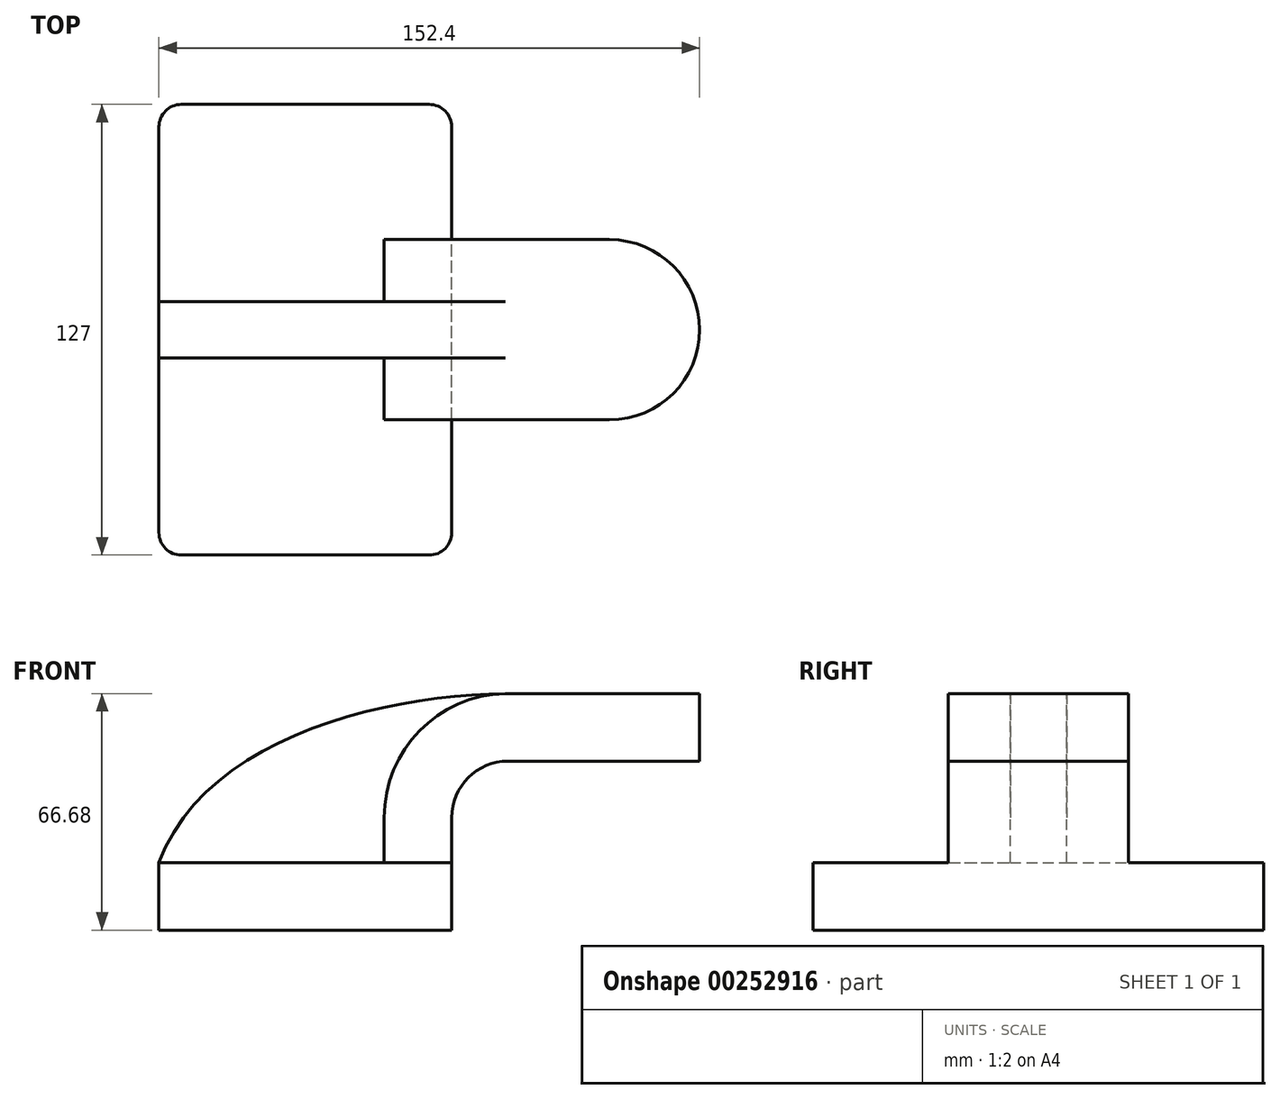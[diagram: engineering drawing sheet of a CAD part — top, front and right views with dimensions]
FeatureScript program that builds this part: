
annotation { "Feature Type Name" : "Feature", "Feature Type Description" : "" }
export const myFeature = defineFeature(function(context is Context, id is Id, definition is map)
    precondition{}
    {
        {
            var Q0;
            Q0=qCreatedBy(makeId("Front.planeOp"),FACE);
            var sketch = newSketch(context, id + "F0", { "sketchPlane" : qUnion([Q0])});
            skLineSegment(sketch, "E0.bottom", {"start": v(41.28, -9.52) * mm, "end": v(-41.28, -9.53) * mm});
            skLineSegment(sketch, "E0.top", {"start": v(41.28, 9.53) * mm, "end": v(-41.28, 9.53) * mm});
            skLineSegment(sketch, "E0.left", {"start": v(41.28, -9.52) * mm, "end": v(41.28, 9.53) * mm});
            skLineSegment(sketch, "E0.right", {"start": v(-41.28, -9.53) * mm, "end": v(-41.28, 9.53) * mm});
            skPoint(sketch, "E0.middle", {"position": v(0, 0) * mm});
            skLineSegment(sketch, "E1.bottom", {"start": v(111.13, 38.1) * mm, "end": v(60.33, 38.1) * mm});
            skLineSegment(sketch, "E1.top", {"start": v(111.13, 66.68) * mm, "end": v(60.33, 66.68) * mm});
            skLineSegment(sketch, "E1.left", {"start": v(111.13, 38.1) * mm, "end": v(111.13, 66.68) * mm});
            skLineSegment(sketch, "E1.right", {"start": v(60.33, 38.1) * mm, "end": v(60.33, 66.67) * mm});
            skPoint(sketch, "E1.middle", {"position": v(85.73, 52.39) * mm});
            skLineSegment(sketch, "E2", {"start": v(41.28, 9.53) * mm, "end": v(41.28, 22.23) * mm});
            skArc(sketch, "E3", {"start": v(41.27, 22.23) * mm, "mid": v(45.92, 33.45) * mm, "end": v(57.15, 38.1) * mm});
            skLineSegment(sketch, "E4", {"start": v(57.15, 38.1) * mm, "end": v(80.61, 38.1) * mm});
            skLineSegment(sketch, "E5.0", {"start": v(57.15, 57.15) * mm, "end": v(80.61, 57.15) * mm});
            skArc(sketch, "E5.1", {"start": v(22.22, 22.23) * mm, "mid": v(32.45, 46.92) * mm, "end": v(57.15, 57.15) * mm});
            skLineSegment(sketch, "E5.2", {"start": v(22.22, 9.53) * mm, "end": v(22.22, 22.23) * mm});
            skFitSpline(sketch, "E6", {"points": [v(-41.28, 9.53) * mm, v(57.15, 57.15) * mm], "startDerivative": vector(39.74, 106.1) * mm, "endDerivative": vector(104.57, 0.93) * mm});
            skLineSegment(sketch, "E7", {"start": v(85.73, 66.68) * mm, "end": v(85.73, 38.1) * mm});
            skLineSegment(sketch, "E8", {"start": v(80.61, 57.15) * mm, "end": v(85.73, 57.15) * mm});
            skLineSegment(sketch, "E9", {"start": v(80.61, 38.1) * mm, "end": v(85.73, 38.1) * mm});
            skSolve(sketch);
        }
        {
            var Q0;
            Q0=makeQuery(id+"F0.imprint","IMPRINT",FACE,{"disambiguationData":[TD([[makeQuery(id+"F0.imprint","IMPRINT",EDGE,{"derivedFrom":sQuery(id+"F0.wireOp",EDGE,"E0.bottom")}),-1.0]])]});
            extrude(context, id + "F1", {"entities" : qUnion([Q0]), "endBound" : BoundingType.SYMMETRIC, "depth" : 127 * mm});
        }
        {
            var Q0;
            {var subQ3=sQuery(id+"F0.wireOp",EDGE,"E5.2");Q0=makeQuery(id+"F0.imprint","IMPRINT",FACE,{"disambiguationData":[TD([[makeQuery(id+"F0.imprint","IMPRINT",EDGE,{"derivedFrom":subQ3}),1.0]])]});}
            extrude(context, id + "F2", {"entities" : qUnion([Q0]), "operationType" : NewBodyOperationType.ADD, "endBound" : BoundingType.SYMMETRIC, "depth" : 15.88 * mm});
        }
        {
            var Q0;
            {var subQ1=sQuery(id+"F0.wireOp",EDGE,"E2");Q0=makeQuery(id+"F0.imprint","IMPRINT",FACE,{"disambiguationData":[TD([[makeQuery(id+"F0.imprint","IMPRINT",EDGE,{"derivedFrom":subQ1}),1.0]])]});}
            var Q1;
            {var subQ2=sQuery(id+"F0.wireOp",EDGE,"E8");Q1=makeQuery(id+"F0.imprint","IMPRINT",FACE,{"disambiguationData":[TD([[makeQuery(id+"F0.imprint","IMPRINT",EDGE,{"derivedFrom":subQ2}),-1.0]])]});}
            extrude(context, id + "F3", {"entities" : qUnion([Q0, Q1]), "operationType" : NewBodyOperationType.ADD, "endBound" : BoundingType.SYMMETRIC, "depth" : 50.8 * mm});
        }
        {
            var Q0;
            {var subQ5=sQuery(id+"F0.wireOp",EDGE,"E1.bottom");Q0=makeQuery(id+"F0.imprint","IMPRINT",FACE,{"disambiguationData":[TD([[makeQuery(id+"F0.imprint","IMPRINT",EDGE,{"derivedFrom":subQ5}),-1.0]])]});}
            var Q1;
            Q1=sQuery(id+"F0.wireOp",EDGE,"E7");
            revolve(context, id + "F4", {"operationType" : NewBodyOperationType.ADD, "entities" : qUnion([Q0]), "axis" : qUnion([Q1]), "revolveType" : RevolveType.FULL});
        }
        {
            var Q0;
            Q0=makeQuery(id+"F1.opExtrude","CAP_EDGE",EDGE,{"disambiguationData":[OSD([sQuery(id+"F0.wireOp",EDGE,"E0.left")])],"isStart":false});
            var Q1;
            Q1=makeQuery(id+"F1.opExtrude","CAP_EDGE",EDGE,{"disambiguationData":[OSD([sQuery(id+"F0.wireOp",EDGE,"E0.right")])],"isStart":false});
            var Q2;
            Q2=makeQuery(id+"F1.opExtrude","CAP_EDGE",EDGE,{"disambiguationData":[OSD([sQuery(id+"F0.wireOp",EDGE,"E0.right")])],"isStart":true});
            var Q3;
            Q3=makeQuery(id+"F1.opExtrude","CAP_EDGE",EDGE,{"disambiguationData":[OSD([sQuery(id+"F0.wireOp",EDGE,"E0.left")])],"isStart":true});
            fillet(context, id + "F5", {"entities" : qUnion([Q0, Q1, Q2, Q3]), "radius" : 6.35 * mm, "tangentPropagation" : true, "allowEdgeOverflow" : false});
        }
    });
